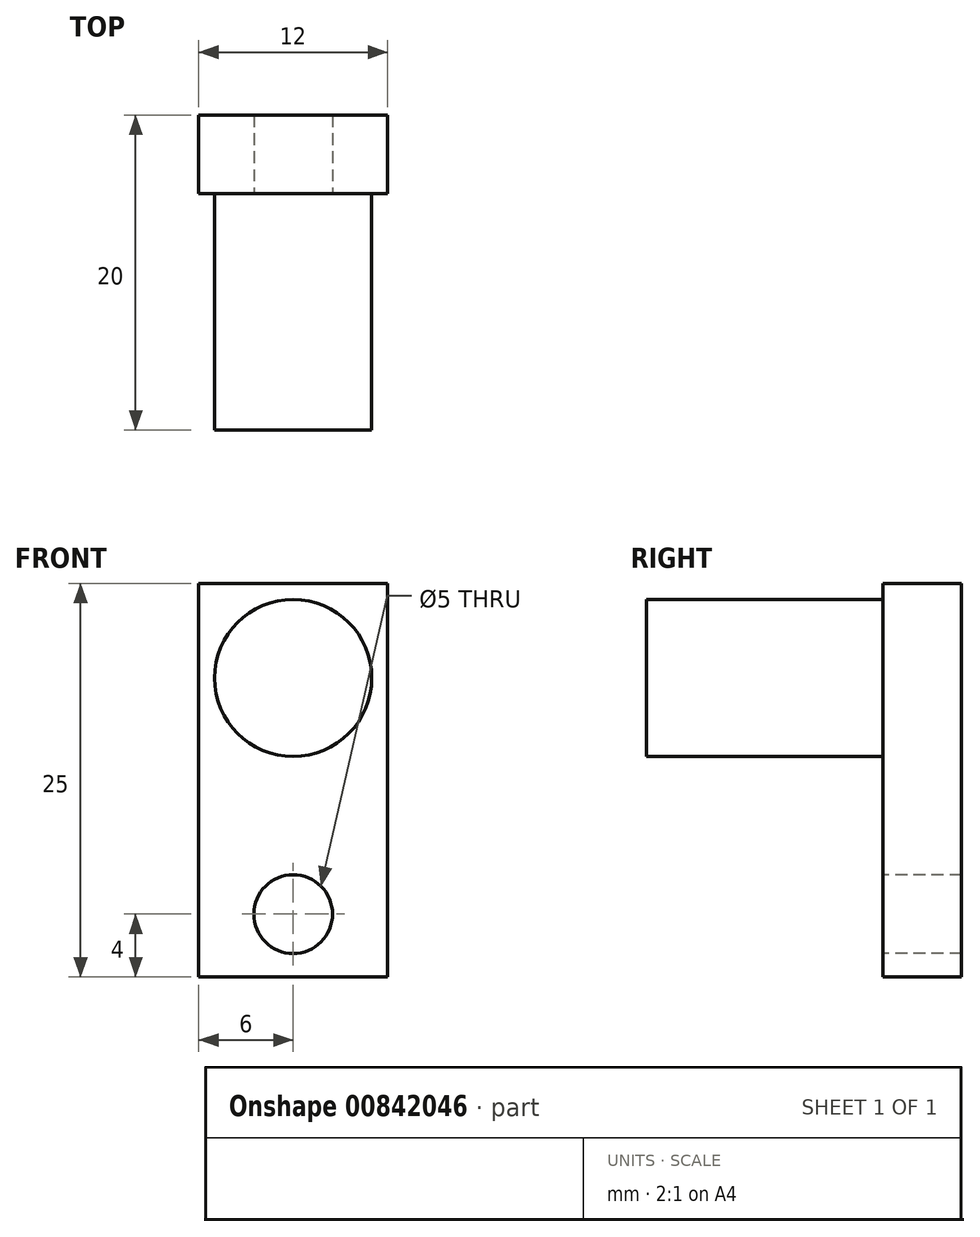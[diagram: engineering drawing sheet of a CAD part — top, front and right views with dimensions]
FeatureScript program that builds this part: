
annotation { "Feature Type Name" : "Feature", "Feature Type Description" : "" }
export const myFeature = defineFeature(function(context is Context, id is Id, definition is map)
    precondition{}
    {
        {
            var Q0;
            Q0=qCreatedBy(makeId("Front.planeOp"),FACE);
            var sketch = newSketch(context, id + "F0", { "sketchPlane" : qUnion([Q0])});
            skLineSegment(sketch, "E0.bottom", {"start": v(0, 0) * mm, "end": v(12, 0) * mm});
            skLineSegment(sketch, "E0.top", {"start": v(0, 25) * mm, "end": v(12, 25) * mm});
            skLineSegment(sketch, "E0.left", {"start": v(0, 0) * mm, "end": v(0, 25) * mm});
            skLineSegment(sketch, "E0.right", {"start": v(12, 0) * mm, "end": v(12, 25) * mm});
            skSolve(sketch);
        }
        {
            var Q0;
            Q0 = qSketchRegion(id + "F0", true);
            extrude(context, id + "F1", {"entities" : qUnion([Q0]), "depth" : 5 * mm, "offsetDistance" : 25 * mm});
        }
        {
            var Q0;
            Q0=makeQuery(id+"F1.opExtrude","CAP_FACE",FACE,{"disambiguationData":[OSD([sQuery(id+"F0.wireOp",EDGE,"E0.bottom"),sQuery(id+"F0.wireOp",EDGE,"E0.top"),sQuery(id+"F0.wireOp",EDGE,"E0.left"),sQuery(id+"F0.wireOp",EDGE,"E0.right")])],"isStart":false});
            var sketch = newSketch(context, id + "F2", { "sketchPlane" : qUnion([Q0])});
            skCircle(sketch, "E1", {"center": v(6, 4) * mm, "radius": 2.5 * mm});
            skSolve(sketch);
        }
        {
            var Q0;
            Q0 = qSketchRegion(id + "F2", true);
            extrude(context, id + "F3", {"entities" : qUnion([Q0]), "operationType" : NewBodyOperationType.REMOVE, "endBound" : BoundingType.THROUGH_ALL, "oppositeDirection" : true, "depth" : 25 * mm, "offsetDistance" : 25 * mm});
        }
        {
            var Q0;
            Q0=makeQuery(id+"F1.opExtrude","CAP_FACE",FACE,{"disambiguationData":[OSD([sQuery(id+"F0.wireOp",EDGE,"E0.bottom"),sQuery(id+"F0.wireOp",EDGE,"E0.top"),sQuery(id+"F0.wireOp",EDGE,"E0.left"),sQuery(id+"F0.wireOp",EDGE,"E0.right")])],"isStart":false});
            var sketch = newSketch(context, id + "F4", { "sketchPlane" : qUnion([Q0])});
            skCircle(sketch, "E2", {"center": v(6, 19) * mm, "radius": 5 * mm});
            skPoint(sketch, "E2.centerSnap0", {"position": v(6, 25) * mm});
            skSolve(sketch);
        }
        {
            var Q0;
            Q0 = qSketchRegion(id + "F4", true);
            extrude(context, id + "F5", {"entities" : qUnion([Q0]), "operationType" : NewBodyOperationType.ADD, "depth" : 15 * mm, "offsetDistance" : 25 * mm});
        }
    });
